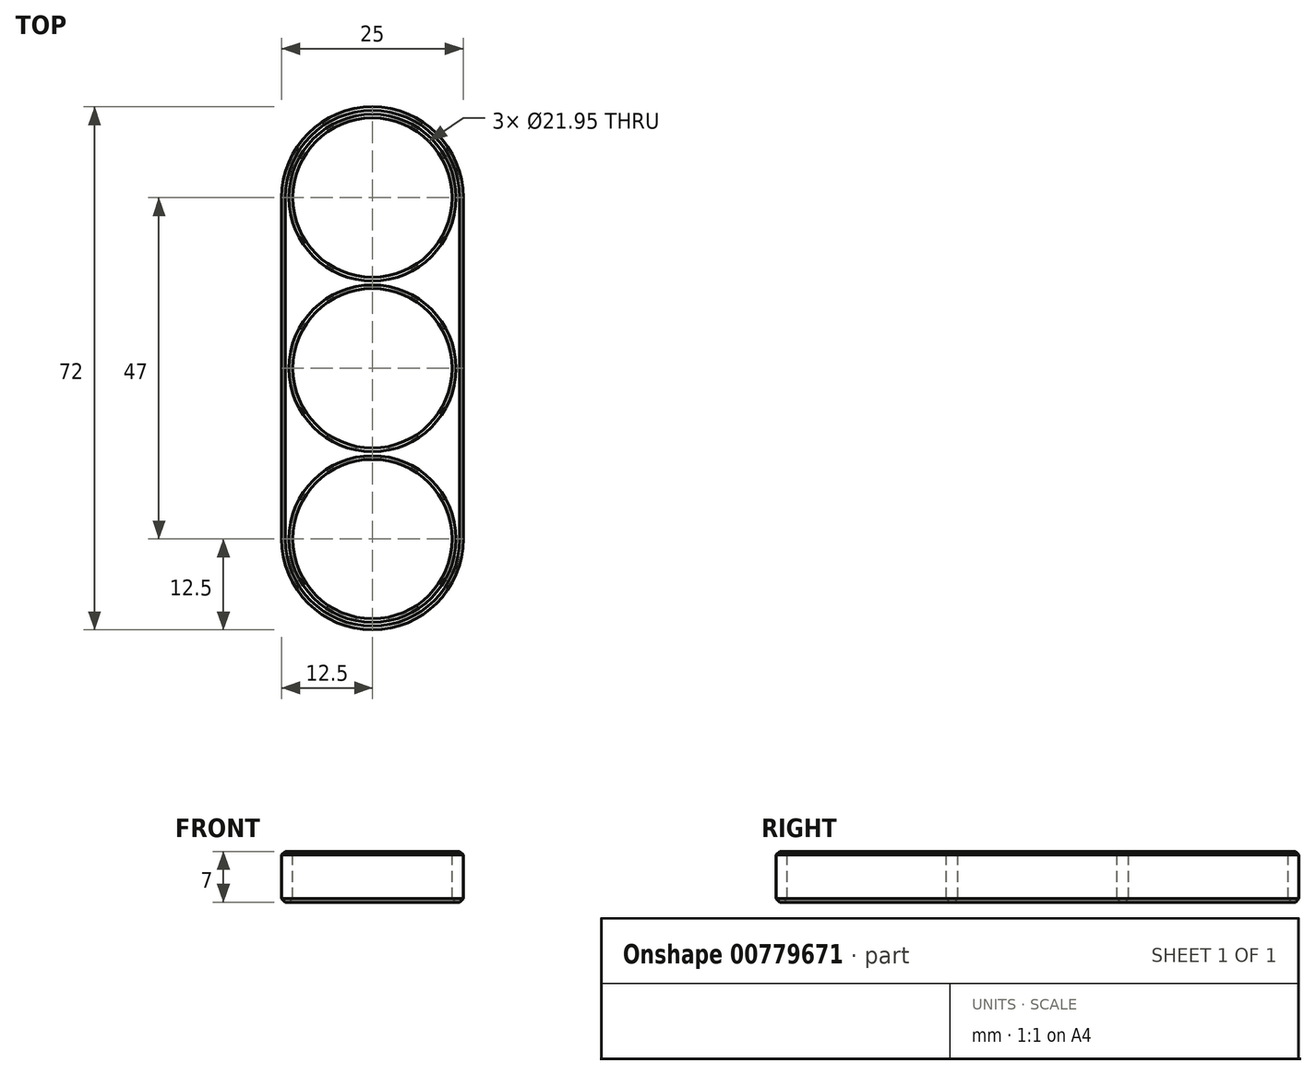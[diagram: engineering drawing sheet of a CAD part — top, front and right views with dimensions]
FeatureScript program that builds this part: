
annotation { "Feature Type Name" : "Feature", "Feature Type Description" : "" }
export const myFeature = defineFeature(function(context is Context, id is Id, definition is map)
    precondition{}
    {
        {
            var Q0;
            Q0=qCreatedBy(makeId("Top.planeOp"),FACE);
            var sketch = newSketch(context, id + "F0", { "sketchPlane" : qUnion([Q0])});
            skCircle(sketch, "E0", {"center": v(0, 0) * mm, "radius": 10.97 * mm});
            skCircle(sketch, "E1", {"center": v(0, 23.5) * mm, "radius": 10.97 * mm});
            skLineSegment(sketch, "E2", {"start": v(-18.93, 0) * mm, "end": v(27.84, 0) * mm, "construction": true});
            skCircle(sketch, "E3.MirrorC", {"center": v(0, -23.5) * mm, "radius": 10.97 * mm});
            skArc(sketch, "E4", {"start": v(12.5, 23.5) * mm, "mid": v(0, 36) * mm, "end": v(-12.5, 23.5) * mm});
            skArc(sketch, "E5.MirrorC", {"start": v(12.5, -23.5) * mm, "mid": v(0, -36) * mm, "end": v(-12.5, -23.5) * mm});
            skLineSegment(sketch, "E6", {"start": v(-12.5, 23.5) * mm, "end": v(-12.5, -23.5) * mm});
            skLineSegment(sketch, "E7", {"start": v(0, 38.63) * mm, "end": v(0, -40.79) * mm, "construction": true});
            skLineSegment(sketch, "E8.MirrorCS", {"start": v(-25, 38.63) * mm, "end": v(-25, -40.79) * mm, "construction": true});
            skLineSegment(sketch, "E9", {"start": v(12.5, -23.5) * mm, "end": v(12.5, 23.5) * mm});
            skSolve(sketch);
        }
        {
            var Q0;
            Q0=qSketchRegion(id+"F0",true);
            extrude(context, id + "F1", {"entities" : qUnion([Q0]), "endBound" : BoundingType.SYMMETRIC, "oppositeDirection" : true, "depth" : 7 * mm, "offsetDistance" : 25 * mm});
        }
        {
            var Q0;
            Q0=makeQuery(id+"F1.opExtrude","CAP_FACE",FACE,{"disambiguationData":[OSD([sQuery(id+"F0.wireOp",EDGE,"E0"),sQuery(id+"F0.wireOp",EDGE,"E1"),sQuery(id+"F0.wireOp",EDGE,"E3.MirrorC"),sQuery(id+"F0.wireOp",EDGE,"E4"),sQuery(id+"F0.wireOp",EDGE,"E5.MirrorC"),sQuery(id+"F0.wireOp",EDGE,"E6"),sQuery(id+"F0.wireOp",EDGE,"E9")])],"isStart":true});
            var Q1;
            Q1=makeQuery(id+"F1.opExtrude","CAP_FACE",FACE,{"disambiguationData":[OSD([sQuery(id+"F0.wireOp",EDGE,"E0"),sQuery(id+"F0.wireOp",EDGE,"E1"),sQuery(id+"F0.wireOp",EDGE,"E3.MirrorC"),sQuery(id+"F0.wireOp",EDGE,"E4"),sQuery(id+"F0.wireOp",EDGE,"E5.MirrorC"),sQuery(id+"F0.wireOp",EDGE,"E6"),sQuery(id+"F0.wireOp",EDGE,"E9")])],"isStart":false});
            chamfer(context, id + "F2", {"entities" : qUnion([Q0, Q1]), "width" : 0.5 * mm, "tangentPropagation" : true});
        }
    });
